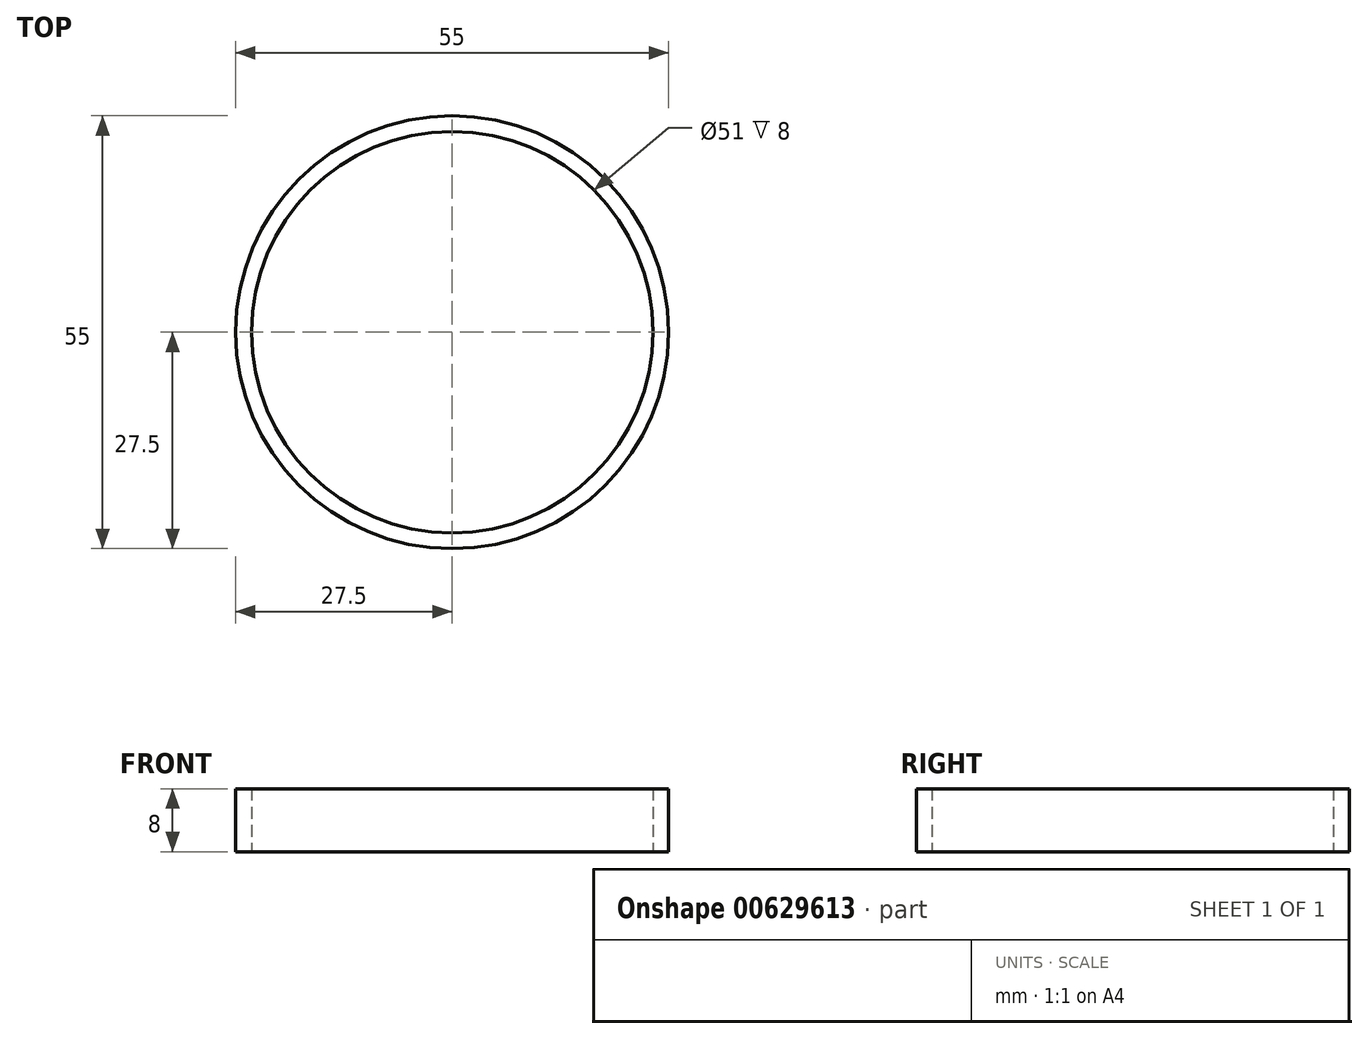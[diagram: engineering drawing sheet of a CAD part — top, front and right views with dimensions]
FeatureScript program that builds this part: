
annotation { "Feature Type Name" : "Feature", "Feature Type Description" : "" }
export const myFeature = defineFeature(function(context is Context, id is Id, definition is map)
    precondition{}
    {
        {
            var Q0;
            Q0=qCreatedBy(makeId("Top.planeOp"),FACE);
            var sketch = newSketch(context, id + "F0", { "sketchPlane" : qUnion([Q0])});
            skCircle(sketch, "E0", {"center": v(0, 0) * mm, "radius": 25.5 * mm});
            skCircle(sketch, "E1", {"center": v(0, 0) * mm, "radius": 27.5 * mm});
            skSolve(sketch);
        }
        {
            var Q0;
            Q0 = qSketchRegion(id + "F0", true);
            extrude(context, id + "F1", {"entities" : qUnion([Q0]), "depth" : 8 * mm, "offsetDistance" : 25 * mm});
        }
    });
